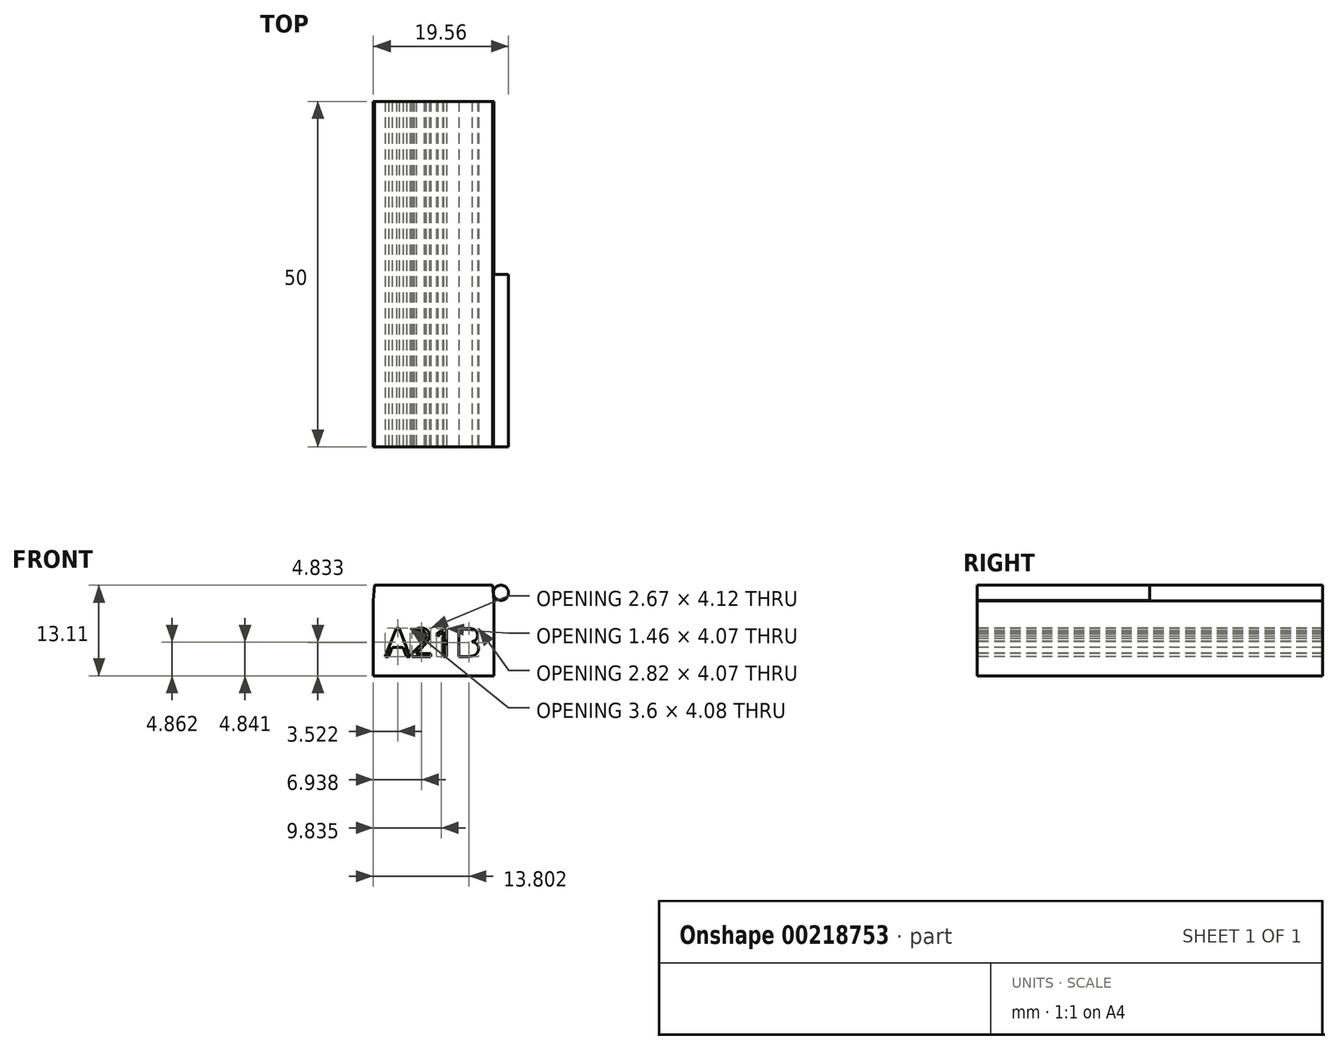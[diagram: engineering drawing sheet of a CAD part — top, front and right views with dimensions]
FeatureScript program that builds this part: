
annotation { "Feature Type Name" : "Feature", "Feature Type Description" : "" }
export const myFeature = defineFeature(function(context is Context, id is Id, definition is map)
    precondition{}
    {
        {
            var Q0;
            Q0=qCreatedBy(makeId("Front.planeOp"),FACE);
            var sketch = newSketch(context, id + "F0", { "sketchPlane" : qUnion([Q0])});
            skLineSegment(sketch, "E0.bottom", {"start": v(0, 0) * mm, "end": v(17.47, 0) * mm});
            skLineSegment(sketch, "E0.top", {"start": v(0.2, 13.1) * mm, "end": v(17.26, 13.1) * mm});
            skLineSegment(sketch, "E0.left", {"start": v(0, 0) * mm, "end": v(0, 10.8) * mm});
            skLineSegment(sketch, "E0.right", {"start": v(17.47, 0) * mm, "end": v(17.47, 10.8) * mm});
            skLineSegment(sketch, "E1", {"start": v(8.73, -1.97) * mm, "end": v(8.73, 16.15) * mm, "construction": true});
            skPoint(sketch, "E2.orphan", {"position": v(8.73, 15) * mm});
            skLineSegment(sketch, "E3", {"start": v(17.26, 13.11) * mm, "end": v(17.47, 10.8) * mm});
            skLineSegment(sketch, "E4", {"start": v(17.26, 13.1) * mm, "end": v(20.02, 13.1) * mm, "construction": true});
            skCircle(sketch, "E5", {"center": v(18.46, 12) * mm, "radius": 1.1 * mm});
            skCircle(sketch, "E6.MirrorC", {"center": v(-1, 12) * mm, "radius": 1.1 * mm});
            skLineSegment(sketch, "E7.MirrorCS", {"start": v(0, 13.1) * mm, "end": v(-2.56, 13.1) * mm, "construction": true});
            skLineSegment(sketch, "E8.MirrorCS", {"start": v(0.2, 13.1) * mm, "end": v(0, 10.8) * mm});
            skPoint(sketch, "E9.orphan", {"position": v(0.2, 13.1) * mm});
            skLineSegment(sketch, "E10", {"start": v(-2.1, 12) * mm, "end": v(-2.1, 10.02) * mm, "construction": true});
            skLineSegment(sketch, "E11.MirrorCS", {"start": v(19.56, 12.01) * mm, "end": v(19.56, 10.02) * mm, "construction": true});
            skText(sketch, "E12", { "text": "A21B", "fontName": "OpenSans-Regular.ttf"});
            const initialGuessF0  = {"E12": [0.00172, 0.0028, 1, 0, 0.0041]};
            skSetInitialGuess(sketch, initialGuessF0);
            skSolve(sketch);
        }
        {
            var Q0;
            Q0=makeQuery(id+"F0.imprint","IMPRINT",FACE,{"disambiguationData":[TD([[makeQuery(id+"F0.imprint","IMPRINT",EDGE,{"derivedFrom":sQuery(id+"F0.wireOp",EDGE,"E0.bottom")}),1.0]])]});
            extrude(context, id + "F1", {"entities" : qUnion([Q0]), "oppositeDirection" : true, "depth" : 50 * mm});
        }
        {
            var Q0;
            Q0=makeQuery(id+"F0.imprint","IMPRINT",FACE,{"disambiguationData":[TD([[makeQuery(id+"F0.imprint","IMPRINT",EDGE,{"derivedFrom":sQuery(id+"F0.wireOp",EDGE,"E6.MirrorC")}),-1.0]])]});
            var Q1;
            Q1=makeQuery(id+"F0.imprint","IMPRINT",FACE,{"disambiguationData":[TD([[makeQuery(id+"F0.imprint","IMPRINT",EDGE,{"derivedFrom":sQuery(id+"F0.wireOp",EDGE,"E5")}),1.0]])]});
            extrude(context, id + "F2", {"entities" : qUnion([Q0, Q1]), "operationType" : NewBodyOperationType.ADD, "oppositeDirection" : true, "depth" : 25 * mm});
        }
    });
